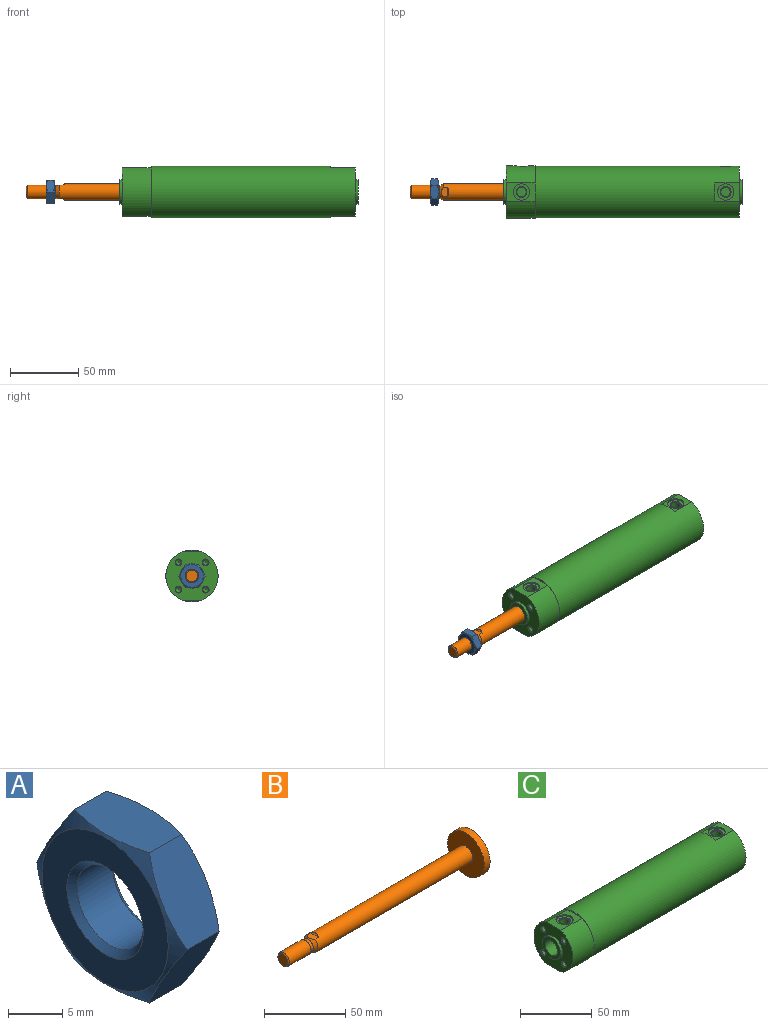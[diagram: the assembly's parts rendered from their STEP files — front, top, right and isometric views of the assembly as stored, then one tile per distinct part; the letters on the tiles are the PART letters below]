
ASSEMBLY  parts=3 mates=2
PART A: 13 faces, bbox 6x19.6x19.6 mm
  f0: plane 16.5x16.5mm, normal (-1,0,0), area 135.3mm2, adj f1,f2
  f1: cone r=0mm half-angle=60deg, axis (1,0,0), area 42.1mm2, adj f0,f3,f4,f5,f6,f7,f8
  f2: cone r=0mm half-angle=45deg, axis (-1,0,0), area 28mm2, adj f0,f9
  f3: plane 8.5x5.72mm, normal (0,-0.87,0.5), area 50.9mm2, adj f1,f4,f8,f10
  f4: plane 8.5x5.72mm, normal (0,-0.87,-0.5), area 50.9mm2, adj f1,f3,f5,f10
  f5: plane 9.82x5.72mm, normal (0,0,-1), area 50.9mm2, adj f1,f4,f6,f10
  f6: plane 8.5x5.72mm, normal (0,0.87,-0.5), area 50.9mm2, adj f1,f5,f7,f10
  f7: plane 8.5x5.72mm, normal (0,0.87,0.5), area 50.9mm2, adj f1,f6,f8,f10
  f8: plane 9.82x5.72mm, normal (0,0,1), area 50.9mm2, adj f1,f3,f7,f10
  f9: cylinder r=4.32mm len=8.65mm, axis (1,0,0), area 126.2mm2, adj f2,f11
  f10: cone r=0mm half-angle=60deg, axis (-1,0,0), area 42.1mm2, adj f3,f4,f5,f6,f7,f8,f12
  f11: cone r=0mm half-angle=45deg, axis (1,0,0), area 28mm2, adj f9,f12
  f12: plane 16.5x16.5mm, normal (1,0,0), area 135.3mm2, adj f10,f11
PART B: 14 faces, bbox 164x32x32 mm
  f0: plane 8.47x8.47mm, normal (-1,0,0), area 56.3mm2, adj f1
  f1: cone r=0mm half-angle=45deg, axis (1,0,0), area 31.5mm2, adj f0,f3
  f2: plane 32x32mm, normal (1,0,0), area 804.2mm2, adj f4
  f3: cylinder r=5mm len=18.73mm, axis (1,0,0), area 588.5mm2, adj f1,f5
  f4: cylinder r=16mm len=32mm, axis (1,0,0), area 502.7mm2, adj f2,f7
  f5: plane 10x10mm, normal (1,0,0), area 13.5mm2, adj f3,f9
  f6: plane 6.63x1mm, normal (-0.71,0,-0.71), area 6.4mm2, adj f10,f12
  f7: plane 32x32mm, normal (-1,0,0), area 691.2mm2, adj f4,f12
  f8: plane 6.63x1mm, normal (-0.71,0,0.71), area 6.4mm2, adj f11,f12
  f9: cylinder r=4.55mm len=9.1mm, axis (1,0,0), area 71.5mm2, adj f5,f13
  f10: plane 6.63x4.72mm, normal (0,0,-1), area 27.3mm2, adj f6,f12,f13
  f11: plane 6.63x4.72mm, normal (0,0,1), area 27.3mm2, adj f8,f12,f13
  f12: cylinder r=6mm len=134.49mm, axis (1,0,0), area 5018.8mm2, adj f6,f7,f8,f10,f11,f13
  f13: cone r=0mm half-angle=30deg, axis (1,0,0), area 78.1mm2, adj f9,f10,f11,f12
PART C: 73 faces, bbox 175x38.4x38 mm
  f0: plane 32x32mm, normal (-1,0,0), area 804.2mm2, adj f1
  f1: cylinder r=16mm len=105mm, axis (1,0,0), area 10555.8mm2, adj f0,f3
  f2: plane 6.92x6.92mm, normal (0,0,-1), area 37.6mm2, adj f7
  f3: plane 32x32mm, normal (1,0,0), area 691.2mm2, adj f1,f12
  f4: plane 6.92x6.92mm, normal (0,0,1), area 37.6mm2, adj f13
  f5: plane 6.92x6.92mm, normal (0,0,1), area 37.6mm2, adj f14
  f6: plane 6.92x6.92mm, normal (0,0,-1), area 37.6mm2, adj f15
  f7: cylinder r=3.46mm len=6.96mm, axis (0,0,-1), area 151.2mm2, adj f2,f16
  f8: cone r=0mm half-angle=60deg, axis (-1,0,0), area 15.5mm2, adj f18
  f9: cone r=0mm half-angle=60deg, axis (-1,0,0), area 15.5mm2, adj f19
  f10: cone r=0mm half-angle=60deg, axis (-1,0,0), area 15.5mm2, adj f20
  f11: cone r=0mm half-angle=60deg, axis (-1,0,0), area 15.5mm2, adj f21
  f12: cylinder r=6mm len=21mm, axis (1,0,0), area 791.7mm2, adj f3,f22
  f13: cylinder r=3.46mm len=6.96mm, axis (0,0,-1), area 151.2mm2, adj f4,f23
  f14: cylinder r=3.46mm len=6.96mm, axis (0,0,-1), area 151.2mm2, adj f5,f24
  f15: cylinder r=3.46mm len=6.96mm, axis (0,0,-1), area 151.2mm2, adj f6,f29
  f16: cone r=0mm half-angle=45deg, axis (0,0,-1), area 17.9mm2, adj f7,f30
  f17: cone r=0mm half-angle=60deg, axis (0,1,0), area 66.5mm2, adj f31
  f18: cylinder r=2.07mm len=7.57mm, axis (1,0,0), area 98.3mm2, adj f8,f32
  f19: cylinder r=2.07mm len=7.57mm, axis (1,0,0), area 98.3mm2, adj f9,f33
  f20: cylinder r=2.07mm len=7.57mm, axis (1,0,0), area 98.3mm2, adj f10,f34
  f21: cylinder r=2.07mm len=7.57mm, axis (1,0,0), area 98.3mm2, adj f11,f35
  f22: plane 18x18mm, normal (-1,0,0), area 141.4mm2, adj f12,f36
  f23: cone r=0mm half-angle=45deg, axis (0,0,1), area 17.9mm2, adj f13,f37
  f24: cone r=0mm half-angle=45deg, axis (0,0,1), area 17.9mm2, adj f14,f38
  f25: cone r=0mm half-angle=60deg, axis (1,0,0), area 15.5mm2, adj f40
  f26: cone r=0mm half-angle=60deg, axis (1,0,0), area 15.5mm2, adj f41
  f27: cone r=0mm half-angle=60deg, axis (1,0,0), area 15.5mm2, adj f42
  f28: cone r=0mm half-angle=60deg, axis (1,0,0), area 15.5mm2, adj f43
  f29: cone r=0mm half-angle=45deg, axis (0,0,-1), area 17.9mm2, adj f15,f44
  f30: plane 12x12mm, normal (0,0,-1), area 62.8mm2, adj f16,f45
  f31: cylinder r=4.28mm len=8.57mm, axis (0,-1,0), area 205mm2, adj f17,f46
  f32: cone r=0mm half-angle=45deg, axis (-1,0,0), area 8.8mm2, adj f18,f47
  f33: cone r=0mm half-angle=45deg, axis (-1,0,0), area 8.8mm2, adj f19,f47
  f34: cone r=0mm half-angle=45deg, axis (-1,0,0), area 8.8mm2, adj f20,f47
  f35: cone r=0mm half-angle=45deg, axis (-1,0,0), area 8.8mm2, adj f21,f47
  f36: cylinder r=9mm len=18mm, axis (1,0,0), area 113.1mm2, adj f22,f47
  f37: plane 12x12mm, normal (0,0,1), area 62.8mm2, adj f23,f48
  f38: plane 12x12mm, normal (0,0,1), area 62.8mm2, adj f24,f51
  f39: plane 18x18mm, normal (1,0,0), area 254.5mm2, adj f52
  f40: cylinder r=2.07mm len=7.57mm, axis (1,0,0), area 98.3mm2, adj f25,f53
  f41: cylinder r=2.07mm len=7.57mm, axis (1,0,0), area 98.3mm2, adj f26,f54
  f42: cylinder r=2.07mm len=7.57mm, axis (1,0,0), area 98.3mm2, adj f27,f55
  f43: cylinder r=2.07mm len=7.57mm, axis (1,0,0), area 98.3mm2, adj f28,f56
  f44: plane 12x12mm, normal (0,0,-1), area 62.8mm2, adj f29,f57
  f45: cylinder r=6mm len=12mm, axis (0,0,-1), area 37.7mm2, adj f30,f58
  f46: cone r=0mm half-angle=45deg, axis (0,1,0), area 12.7mm2, adj f31,f59
  f47: plane 38.4x35.5mm, normal (-1,0,0), area 796.6mm2, adj f32,f33,f34,f35,f36,f50,f58,f59
  f48: cylinder r=6mm len=12mm, axis (0,0,-1), area 37.7mm2, adj f37,f60
  f49: cone r=0mm half-angle=60deg, axis (0,1,0), area 66.5mm2, adj f61
  f50: cylinder r=19.2mm len=35.5mm, axis (1,0,0), area 951.3mm2, adj f47,f58,f60,f62
  f51: cylinder r=6mm len=12mm, axis (0,0,-1), area 37.7mm2, adj f38,f64
  f52: cylinder r=9mm len=18mm, axis (1,0,0), area 113.1mm2, adj f39,f65
  f53: cone r=0mm half-angle=45deg, axis (1,0,0), area 8.8mm2, adj f40,f65
  f54: cone r=0mm half-angle=45deg, axis (1,0,0), area 8.8mm2, adj f41,f65
  f55: cone r=0mm half-angle=45deg, axis (1,0,0), area 8.8mm2, adj f42,f65
  f56: cone r=0mm half-angle=45deg, axis (1,0,0), area 8.8mm2, adj f43,f65
  f57: cylinder r=6mm len=12mm, axis (0,0,-1), area 37.7mm2, adj f44,f66
  f58: plane 21x14.64mm, normal (0,0,-1), area 194.3mm2, adj f45,f47,f50,f59,f62,f68,f69
  f59: cylinder r=19.2mm len=35.5mm, axis (1,0,0), area 884.2mm2, adj f46,f47,f58,f60,f69
  f60: plane 21x14.64mm, normal (0,0,1), area 194.3mm2, adj f47,f48,f50,f59,f62,f69,f70
  f61: cylinder r=4.28mm len=8.57mm, axis (0,-1,0), area 205mm2, adj f49,f71
  f62: plane 35.5x12.42mm, normal (1,0,0), area 9.1mm2, adj f50,f58,f60,f72
  f63: plane 13.56x1.25mm, normal (1,0,0), area 11.4mm2, adj f64,f72
  f64: plane 18x13.56mm, normal (0,0,1), area 130.9mm2, adj f51,f63,f65,f72
  f65: plane 38x35.5mm, normal (1,0,0), area 778.4mm2, adj f52,f53,f54,f55,f56,f64,f66,f72
  f66: plane 18x13.56mm, normal (0,0,-1), area 130.9mm2, adj f57,f65,f67,f72
  f67: plane 13.56x1.25mm, normal (1,0,0), area 11.4mm2, adj f66,f72
  f68: plane 13.56x1.25mm, normal (-1,0,0), area 11.4mm2, adj f58,f72
  f69: plane 35.5x12.42mm, normal (1,0,0), area 9.1mm2, adj f58,f59,f60,f72
  f70: plane 13.56x1.25mm, normal (-1,0,0), area 11.4mm2, adj f60,f72
  f71: cone r=0mm half-angle=45deg, axis (0,1,0), area 12.6mm2, adj f61,f72
  f72: cylinder r=19mm len=150mm, axis (1,0,0), area 17341.1mm2, adj f62,f63,f64,f65,f66,f67,f68,f69
PLACE A t=(-52.87,-31.79,66.9)mm
PLACE B t=(-30.87,-31.79,66.9)mm
PLACE C t=(0,-31.79,66.9)mm fixed
MATE slider C.f1 <-> B.f3  axis (1,0,0) through (171,-31.79,66.9)mm
MATE fastened A.f1 <-> B.f1  axis (-1,0,0) through (-55.87,-31.79,66.9)mm
